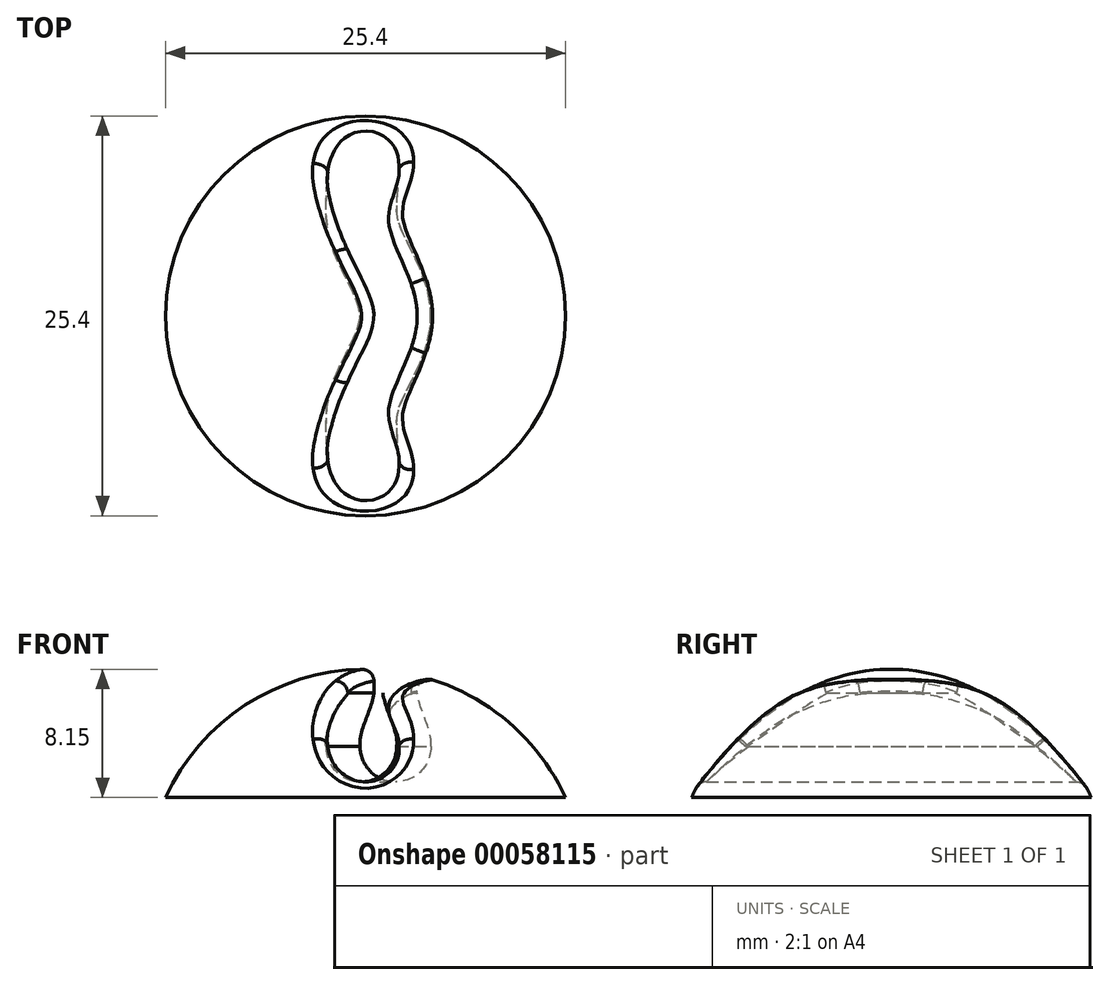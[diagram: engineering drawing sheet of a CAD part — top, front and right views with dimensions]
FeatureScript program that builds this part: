
annotation { "Feature Type Name" : "Feature", "Feature Type Description" : "" }
export const myFeature = defineFeature(function(context is Context, id is Id, definition is map)
    precondition{}
    {
        {
            var Q0;
            Q0=qCreatedBy(makeId("Front.planeOp"),FACE);
            var sketch = newSketch(context, id + "F0", { "sketchPlane" : qUnion([Q0])});
            skLineSegment(sketch, "E0", {"start": v(0, 0) * mm, "end": v(12.7, 0) * mm});
            skArc(sketch, "E1", {"start": v(12.7, 0) * mm, "mid": v(7.55, 5.94) * mm, "end": v(0, 8.15) * mm});
            skLineSegment(sketch, "E2", {"start": v(0, 8.15) * mm, "end": v(0, 0) * mm});
            skSolve(sketch);
        }
        {
            var Q0;
            Q0=qSketchRegion(id+"F0",true);
            var Q1;
            Q1=sQuery(id+"F0.wireOp",EDGE,"E2");
            revolve(context, id + "F1", {"entities" : qUnion([Q0]), "axis" : qUnion([Q1]), "revolveType" : RevolveType.FULL});
        }
        {
            var Q0;
            Q0=qCreatedBy(makeId("Top.planeOp"),FACE);
            var sketch = newSketch(context, id + "F2", { "sketchPlane" : qUnion([Q0])});
            skCircle(sketch, "E3.0", {"center": v(0, 0) * mm, "radius": 12.7 * mm, "construction": true});
            skFitSpline(sketch, "E4", {"points": [v(0, -12.7) * mm, v(0, -5.08) * mm, v(1.9, 0) * mm, v(0, 5.08) * mm, v(0, 12.7) * mm], "startDerivative": vector(0, 49.17) * mm, "endDerivative": vector(0, 49.17) * mm});
            skSolve(sketch);
        }
        {
            var Q0;
            Q0=qCreatedBy(makeId("Front.planeOp"),FACE);
            cPlane(context, id + "F3", {"entities" : qUnion([Q0]), "cplaneType" : CPlaneType.OFFSET, "offset" : 12.7 * mm, "width" : 152.4 * mm, "height" : 152.4 * mm});
        }
        {
            var Q0;
            Q0=qCreatedBy(id+"F3.planeOp",FACE);
            var sketch = newSketch(context, id + "F4", { "sketchPlane" : qUnion([Q0])});
            skLineSegment(sketch, "E5", {"start": v(0, 8.15) * mm, "end": v(0, 0) * mm, "construction": true});
            skCircle(sketch, "E6", {"center": v(0, 3.25) * mm, "radius": 2.25 * mm});
            skFitSpline(sketch, "E7", {"points": [v(-2.25, 3.25) * mm, v(-1.38, 6.64) * mm, v(-1.94, 8.01) * mm], "startDerivative": vector(-0.69, 4.66) * mm, "endDerivative": vector(-3.55, -0.44) * mm});
            skFitSpline(sketch, "E8.MirrorCS", {"points": [v(2.25, 3.25) * mm, v(1.38, 6.64) * mm, v(1.94, 8.01) * mm], "startDerivative": vector(0.69, 4.66) * mm, "endDerivative": vector(3.55, -0.44) * mm});
            skLineSegment(sketch, "E9", {"start": v(-1.38, 6.64) * mm, "end": v(-1.38, 8.99) * mm});
            skLineSegment(sketch, "E10", {"start": v(-1.38, 8.99) * mm, "end": v(1.38, 8.99) * mm});
            skLineSegment(sketch, "E11", {"start": v(1.37, 8.99) * mm, "end": v(1.37, 6.64) * mm});
            skSolve(sketch);
        }
        {
            var Q0;
            Q0=qSketchRegion(id+"F4",true);
            var Q1;
            Q1=qConstructionFilter(qBodyType(qCreatedBy(id+"F2",EDGE),BodyType.WIRE),ConstructionObject.NO);
            sweep(context, id + "F5", {"operationType" : NewBodyOperationType.REMOVE, "profiles" : qUnion([Q0]), "path" : qUnion([Q1])});
        }
        {
            var Q0;
            Q0=makeQuery(id+"F5.boolean.opBoolean","INTERSECT",EDGE,{"disambiguationData":[OD(1.0)],"derivedFrom":[makeQuery(id+"F1.opRevolve","SWEPT_FACE",FACE,{"disambiguationData":[OSD([sQuery(id+"F0.wireOp",EDGE,"E1")])]}),makeQuery(id+"F5.opSweep","SWEPT_FACE",FACE,{"disambiguationData":[OSD([sQuery(id+"F2.wireOp",EDGE,"E4"),sQuery(id+"F4.wireOp",EDGE,"E7")])]})]});
            var Q1;
            Q1=makeQuery(id+"F5.boolean.opBoolean","INTERSECT",EDGE,{"derivedFrom":[makeQuery(id+"F1.opRevolve","SWEPT_FACE",FACE,{"disambiguationData":[OSD([sQuery(id+"F0.wireOp",EDGE,"E1")])]}),makeQuery(id+"F5.opSweep","SWEPT_FACE",FACE,{"disambiguationData":[OSD([sQuery(id+"F2.wireOp",EDGE,"E4"),sQuery(id+"F4.wireOp",EDGE,"E9")])]})]});
            var Q2;
            Q2=makeQuery(id+"F5.boolean.opBoolean","INTERSECT",EDGE,{"disambiguationData":[OD(0.0)],"derivedFrom":[makeQuery(id+"F1.opRevolve","SWEPT_FACE",FACE,{"disambiguationData":[OSD([sQuery(id+"F0.wireOp",EDGE,"E1")])]}),makeQuery(id+"F5.opSweep","SWEPT_FACE",FACE,{"disambiguationData":[OSD([sQuery(id+"F2.wireOp",EDGE,"E4"),sQuery(id+"F4.wireOp",EDGE,"E7")])]})]});
            var Q3;
            Q3=makeQuery(id+"F5.boolean.opBoolean","INTERSECT",EDGE,{"disambiguationData":[OD(0.0)],"derivedFrom":[makeQuery(id+"F1.opRevolve","SWEPT_FACE",FACE,{"disambiguationData":[OSD([sQuery(id+"F0.wireOp",EDGE,"E1")])]}),makeQuery(id+"F5.opSweep","SWEPT_FACE",FACE,{"disambiguationData":[OSD([sQuery(id+"F2.wireOp",EDGE,"E4"),sQuery(id+"F4.wireOp",EDGE,"E6")])]})]});
            var Q4;
            Q4=makeQuery(id+"F5.boolean.opBoolean","INTERSECT",EDGE,{"disambiguationData":[OD(0.0)],"derivedFrom":[makeQuery(id+"F1.opRevolve","SWEPT_FACE",FACE,{"disambiguationData":[OSD([sQuery(id+"F0.wireOp",EDGE,"E1")])]}),makeQuery(id+"F5.opSweep","SWEPT_FACE",FACE,{"disambiguationData":[OSD([sQuery(id+"F2.wireOp",EDGE,"E4"),sQuery(id+"F4.wireOp",EDGE,"E8.MirrorCS")])]})]});
            var Q5;
            Q5=makeQuery(id+"F5.boolean.opBoolean","INTERSECT",EDGE,{"derivedFrom":[makeQuery(id+"F1.opRevolve","SWEPT_FACE",FACE,{"disambiguationData":[OSD([sQuery(id+"F0.wireOp",EDGE,"E1")])]}),makeQuery(id+"F5.opSweep","SWEPT_FACE",FACE,{"disambiguationData":[OSD([sQuery(id+"F2.wireOp",EDGE,"E4"),sQuery(id+"F4.wireOp",EDGE,"E11")])]})]});
            var Q6;
            Q6=makeQuery(id+"F5.boolean.opBoolean","INTERSECT",EDGE,{"disambiguationData":[OD(1.0)],"derivedFrom":[makeQuery(id+"F1.opRevolve","SWEPT_FACE",FACE,{"disambiguationData":[OSD([sQuery(id+"F0.wireOp",EDGE,"E1")])]}),makeQuery(id+"F5.opSweep","SWEPT_FACE",FACE,{"disambiguationData":[OSD([sQuery(id+"F2.wireOp",EDGE,"E4"),sQuery(id+"F4.wireOp",EDGE,"E8.MirrorCS")])]})]});
            var Q7;
            Q7=makeQuery(id+"F5.boolean.opBoolean","INTERSECT",EDGE,{"disambiguationData":[OD(1.0)],"derivedFrom":[makeQuery(id+"F1.opRevolve","SWEPT_FACE",FACE,{"disambiguationData":[OSD([sQuery(id+"F0.wireOp",EDGE,"E1")])]}),makeQuery(id+"F5.opSweep","SWEPT_FACE",FACE,{"disambiguationData":[OSD([sQuery(id+"F2.wireOp",EDGE,"E4"),sQuery(id+"F4.wireOp",EDGE,"E6")])]})]});
            fillet(context, id + "F6", {"entities" : qUnion([Q0, Q1, Q2, Q3, Q4, Q5, Q6, Q7]), "radius" : 0.75 * mm, "tangentPropagation" : true, "allowEdgeOverflow" : false});
        }
    });
